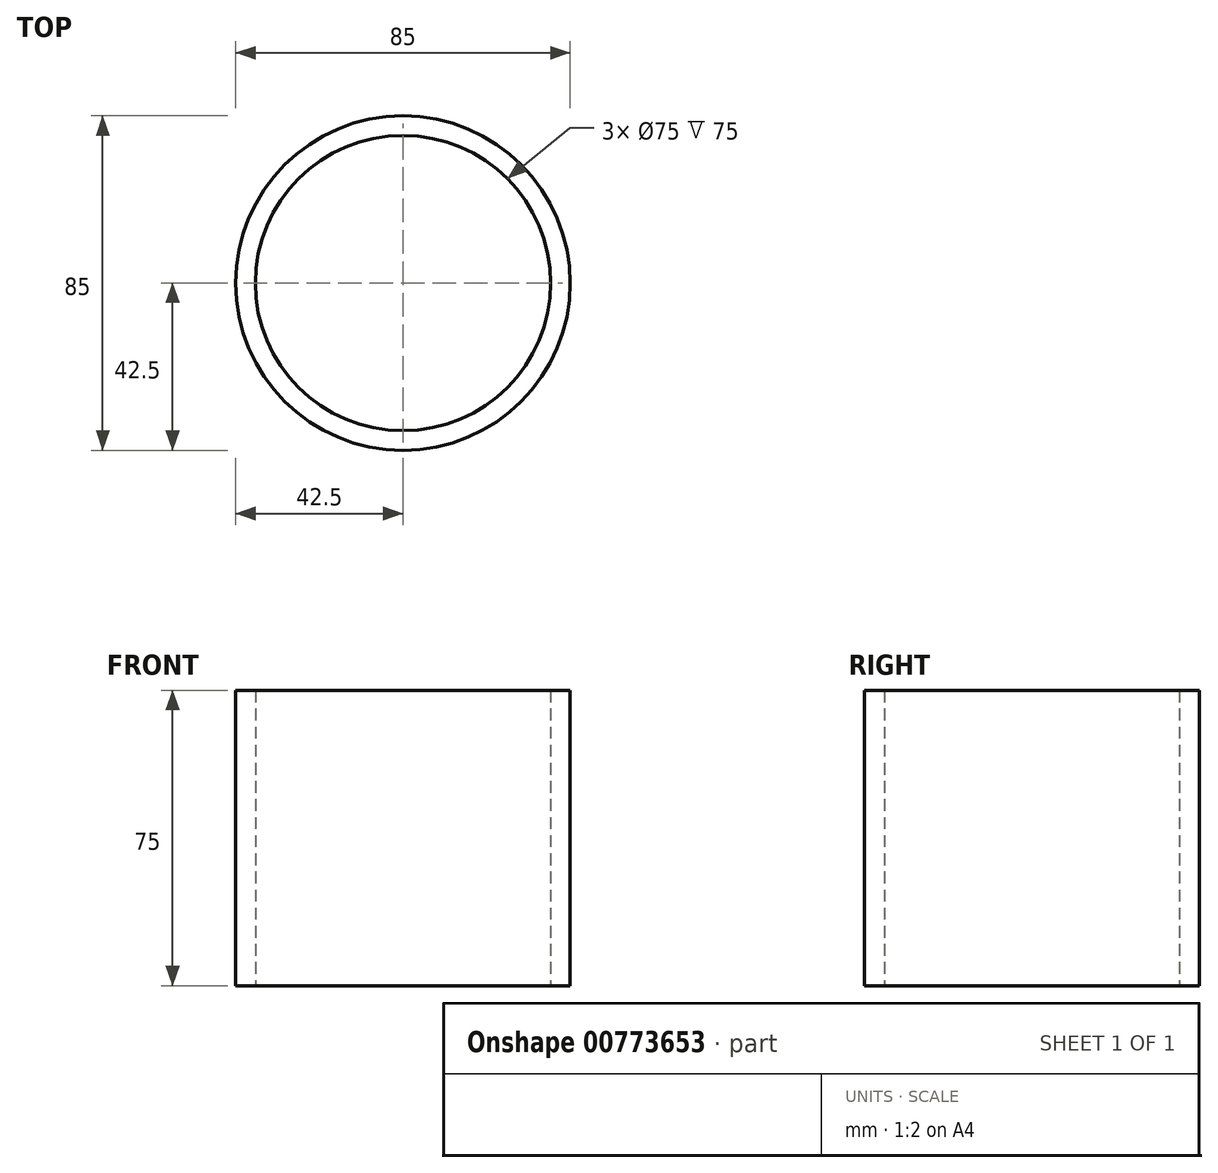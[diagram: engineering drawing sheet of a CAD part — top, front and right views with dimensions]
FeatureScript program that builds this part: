
annotation { "Feature Type Name" : "Feature", "Feature Type Description" : "" }
export const myFeature = defineFeature(function(context is Context, id is Id, definition is map)
    precondition{}
    {
        {
            var Q0;
            Q0=qCreatedBy(makeId("Top.planeOp"),FACE);
            var sketch = newSketch(context, id + "F0", { "sketchPlane" : qUnion([Q0])});
            skCircle(sketch, "E0", {"center": v(0, 0) * mm, "radius": 37.5 * mm});
            skCircle(sketch, "E1", {"center": v(0, 0) * mm, "radius": 42.5 * mm});
            skSolve(sketch);
        }
        {
            var Q0;
            Q0=makeQuery(id+"F0.imprint","IMPRINT",FACE,{"disambiguationData":[TD([[makeQuery(id+"F0.imprint","IMPRINT",EDGE,{"derivedFrom":sQuery(id+"F0.wireOp",EDGE,"E0")}),-1.0]])]});
            extrude(context, id + "F1", {"entities" : qUnion([Q0]), "depth" : 75 * mm, "offsetDistance" : 25.4 * mm});
        }
    });
